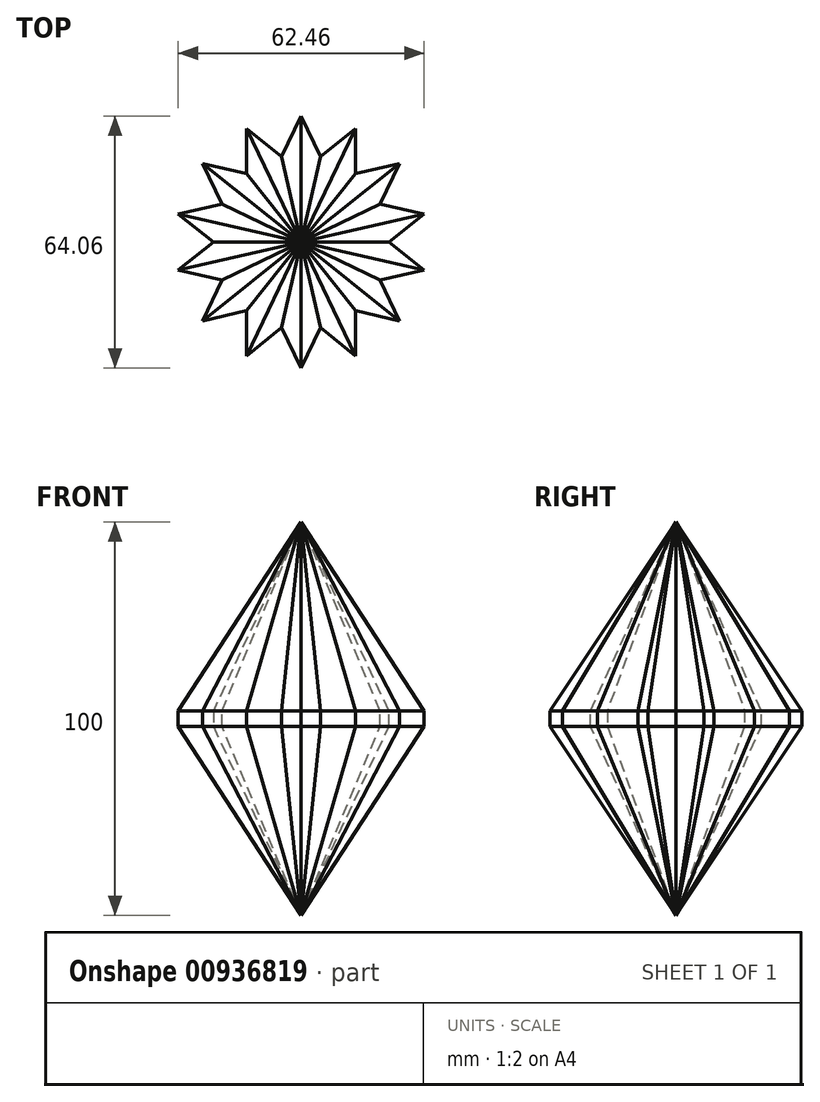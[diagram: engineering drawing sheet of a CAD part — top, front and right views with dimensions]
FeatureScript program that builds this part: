
annotation { "Feature Type Name" : "Feature", "Feature Type Description" : "" }
export const myFeature = defineFeature(function(context is Context, id is Id, definition is map)
    precondition{}
    {
        {
            var Q0;
            Q0=qCreatedBy(makeId("Top.planeOp"),FACE);
            var sketch = newSketch(context, id + "F0", { "sketchPlane" : qUnion([Q0])});
            skCircle(sketch, "E0.cCircle", {"center": v(0, 0) * mm, "radius": 32.03 * mm, "construction": true});
            skLineSegment(sketch, "E0.0", {"start": v(-34.66, -7.91) * mm, "end": v(-27.8, 22.17) * mm, "construction": true});
            skLineSegment(sketch, "E0.1", {"start": v(-27.8, 22.17) * mm, "end": v(0, 35.55) * mm, "construction": true});
            skLineSegment(sketch, "E0.2", {"start": v(0, 35.55) * mm, "end": v(27.8, 22.17) * mm, "construction": true});
            skLineSegment(sketch, "E0.3", {"start": v(27.8, 22.17) * mm, "end": v(34.66, -7.91) * mm, "construction": true});
            skLineSegment(sketch, "E0.4", {"start": v(34.66, -7.91) * mm, "end": v(15.42, -32.03) * mm, "construction": true});
            skLineSegment(sketch, "E0.5", {"start": v(15.42, -32.03) * mm, "end": v(-15.42, -32.03) * mm, "construction": true});
            skLineSegment(sketch, "E0.6", {"start": v(-15.42, -32.03) * mm, "end": v(-34.66, -7.91) * mm, "construction": true});
            skPoint(sketch, "E0.0.midPoint", {"position": v(-31.23, 7.13) * mm});
            skCircle(sketch, "E1.cCircle", {"center": v(0, 0) * mm, "radius": 16 * mm, "construction": true});
            skLineSegment(sketch, "E1.0", {"start": v(-17.32, -3.95) * mm, "end": v(-13.9, 11.08) * mm});
            skLineSegment(sketch, "E1.1", {"start": v(-13.9, 11.08) * mm, "end": v(0, 17.77) * mm, "construction": true});
            skLineSegment(sketch, "E1.2", {"start": v(0, 17.77) * mm, "end": v(13.9, 11.08) * mm});
            skLineSegment(sketch, "E1.3", {"start": v(13.9, 11.08) * mm, "end": v(17.32, -3.95) * mm});
            skLineSegment(sketch, "E1.4", {"start": v(17.32, -3.95) * mm, "end": v(7.7, -16) * mm});
            skLineSegment(sketch, "E1.5", {"start": v(7.7, -16) * mm, "end": v(-7.7, -16) * mm});
            skLineSegment(sketch, "E1.6", {"start": v(-7.7, -16) * mm, "end": v(-17.32, -3.95) * mm});
            skPoint(sketch, "E1.0.midPoint", {"position": v(-15.6, 3.56) * mm});
            skLineSegment(sketch, "E2", {"start": v(0, 17.77) * mm, "end": v(13.9, 28.86) * mm});
            skLineSegment(sketch, "E3", {"start": v(13.9, 28.86) * mm, "end": v(13.9, 11.08) * mm});
            skLineSegment(sketch, "E4", {"start": v(13.9, 11.08) * mm, "end": v(31.23, 7.13) * mm});
            skLineSegment(sketch, "E5", {"start": v(31.23, 7.13) * mm, "end": v(17.32, -3.95) * mm});
            skLineSegment(sketch, "E6", {"start": v(0, 17.77) * mm, "end": v(-13.9, 28.86) * mm});
            skLineSegment(sketch, "E7", {"start": v(-13.9, 28.86) * mm, "end": v(-13.9, 11.08) * mm});
            skLineSegment(sketch, "E8", {"start": v(-13.9, 11.08) * mm, "end": v(-31.23, 7.13) * mm});
            skLineSegment(sketch, "E9", {"start": v(-31.23, 7.13) * mm, "end": v(-17.32, -3.95) * mm});
            skLineSegment(sketch, "E10", {"start": v(-17.32, -3.95) * mm, "end": v(-25.04, -19.97) * mm});
            skLineSegment(sketch, "E11", {"start": v(-25.04, -19.97) * mm, "end": v(-7.7, -16) * mm});
            skLineSegment(sketch, "E12", {"start": v(-7.7, -16) * mm, "end": v(0, -32.03) * mm});
            skLineSegment(sketch, "E13", {"start": v(0, -32.03) * mm, "end": v(7.7, -16) * mm});
            skLineSegment(sketch, "E14", {"start": v(7.7, -16) * mm, "end": v(25.04, -19.97) * mm});
            skLineSegment(sketch, "E15", {"start": v(25.04, -19.97) * mm, "end": v(17.32, -3.95) * mm});
            skSolve(sketch);
        }
        {
            var Q0;
            Q0=qCreatedBy(makeId("Top.planeOp"),FACE);
            cPlane(context, id + "F1", {"entities" : qUnion([Q0]), "cplaneType" : CPlaneType.OFFSET, "offset" : 50 * mm, "width" : 150 * mm, "height" : 150 * mm});
        }
        {
            var Q0;
            Q0=makeQuery(id+"F0.imprint","IMPRINT",FACE,{"disambiguationData":[TD([[makeQuery(id+"F0.imprint","IMPRINT",EDGE,{"derivedFrom":sQuery(id+"F0.wireOp",EDGE,"E1.0")}),-1.0]])]});
            var Q1;
            Q1=makeQuery(id+"F0.imprint","IMPRINT",FACE,{"disambiguationData":[TD([[makeQuery(id+"F0.imprint","IMPRINT",EDGE,{"derivedFrom":sQuery(id+"F0.wireOp",EDGE,"E1.4")}),1.0]])]});
            var Q2;
            Q2=makeQuery(id+"F0.imprint","IMPRINT",FACE,{"disambiguationData":[TD([[makeQuery(id+"F0.imprint","IMPRINT",EDGE,{"derivedFrom":sQuery(id+"F0.wireOp",EDGE,"E1.3")}),1.0]])]});
            var Q3;
            Q3=makeQuery(id+"F0.imprint","IMPRINT",FACE,{"disambiguationData":[TD([[makeQuery(id+"F0.imprint","IMPRINT",EDGE,{"derivedFrom":sQuery(id+"F0.wireOp",EDGE,"E1.5")}),1.0]])]});
            var Q4;
            Q4=makeQuery(id+"F0.imprint","IMPRINT",FACE,{"disambiguationData":[TD([[makeQuery(id+"F0.imprint","IMPRINT",EDGE,{"derivedFrom":sQuery(id+"F0.wireOp",EDGE,"E1.6")}),1.0]])]});
            var Q5;
            Q5=makeQuery(id+"F0.imprint","IMPRINT",FACE,{"disambiguationData":[TD([[makeQuery(id+"F0.imprint","IMPRINT",EDGE,{"derivedFrom":sQuery(id+"F0.wireOp",EDGE,"E1.0")}),1.0]])]});
            var Q6;
            Q6=makeQuery(id+"F0.imprint","IMPRINT",FACE,{"disambiguationData":[TD([[makeQuery(id+"F0.imprint","IMPRINT",EDGE,{"derivedFrom":sQuery(id+"F0.wireOp",EDGE,"E1.2")}),1.0]])]});
            extrude(context, id + "F2", {"entities" : qUnion([Q0, Q1, Q2, Q3, Q4, Q5, Q6]), "depth" : 2 * mm, "offsetDistance" : 25 * mm});
        }
        {
            var Q0;
            Q0=qCreatedBy(id+"F1.planeOp",FACE);
            var sketch = newSketch(context, id + "F3", { "sketchPlane" : qUnion([Q0])});
            skCircle(sketch, "E16", {"center": v(0, 0) * mm, "radius": 2.5 * mm});
            skSolve(sketch);
        }
        {
            var Q1;
            Q1=sQuery(id+"F3.wireOp",VERTEX,"E16.center");
            var Q2;
            Q2=makeQuery(id+"F2.opExtrude","CAP_FACE",FACE,{"disambiguationData":[OSD([sQuery(id+"F0.wireOp",EDGE,"E2"),sQuery(id+"F0.wireOp",EDGE,"E3"),sQuery(id+"F0.wireOp",EDGE,"E4"),sQuery(id+"F0.wireOp",EDGE,"E5"),sQuery(id+"F0.wireOp",EDGE,"E6"),sQuery(id+"F0.wireOp",EDGE,"E7"),sQuery(id+"F0.wireOp",EDGE,"E8"),sQuery(id+"F0.wireOp",EDGE,"E9"),sQuery(id+"F0.wireOp",EDGE,"E10"),sQuery(id+"F0.wireOp",EDGE,"E11"),sQuery(id+"F0.wireOp",EDGE,"E12"),sQuery(id+"F0.wireOp",EDGE,"E13"),sQuery(id+"F0.wireOp",EDGE,"E14"),sQuery(id+"F0.wireOp",EDGE,"E15")])],"isStart":false});
            loft(context, id + "F4", {"operationType" : NewBodyOperationType.ADD, "sheetProfilesArray" : [{ "sheetProfileEntities" : qUnion([Q1]) }, { "sheetProfileEntities" : qUnion([Q2]) }]});
        }
        {
            var Q0;
            Q0=makeQuery(id+"F2.opExtrude","SWEPT_BODY",BODY,{"disambiguationData":[OSD([sQuery(id+"F0.wireOp",EDGE,"E2"),sQuery(id+"F0.wireOp",EDGE,"E3"),sQuery(id+"F0.wireOp",EDGE,"E4"),sQuery(id+"F0.wireOp",EDGE,"E5"),sQuery(id+"F0.wireOp",EDGE,"E6"),sQuery(id+"F0.wireOp",EDGE,"E7"),sQuery(id+"F0.wireOp",EDGE,"E8"),sQuery(id+"F0.wireOp",EDGE,"E9"),sQuery(id+"F0.wireOp",EDGE,"E10"),sQuery(id+"F0.wireOp",EDGE,"E11"),sQuery(id+"F0.wireOp",EDGE,"E12"),sQuery(id+"F0.wireOp",EDGE,"E13"),sQuery(id+"F0.wireOp",EDGE,"E14"),sQuery(id+"F0.wireOp",EDGE,"E15")])]});
            var Q1;
            Q1=makeQuery(id+"F2.opExtrude","CAP_FACE",FACE,{"disambiguationData":[OSD([sQuery(id+"F0.wireOp",EDGE,"E2"),sQuery(id+"F0.wireOp",EDGE,"E3"),sQuery(id+"F0.wireOp",EDGE,"E4"),sQuery(id+"F0.wireOp",EDGE,"E5"),sQuery(id+"F0.wireOp",EDGE,"E6"),sQuery(id+"F0.wireOp",EDGE,"E7"),sQuery(id+"F0.wireOp",EDGE,"E8"),sQuery(id+"F0.wireOp",EDGE,"E9"),sQuery(id+"F0.wireOp",EDGE,"E10"),sQuery(id+"F0.wireOp",EDGE,"E11"),sQuery(id+"F0.wireOp",EDGE,"E12"),sQuery(id+"F0.wireOp",EDGE,"E13"),sQuery(id+"F0.wireOp",EDGE,"E14"),sQuery(id+"F0.wireOp",EDGE,"E15")])],"isStart":true});
            mirror(context, id + "F5", {"operationType" : NewBodyOperationType.ADD, "entities" : qUnion([Q0]), "mirrorPlane" : qUnion([Q1])});
        }
        {
            var Q0;
            Q0=makeQuery(id+"F2.opExtrude","SWEPT_BODY",BODY,{"disambiguationData":[OSD([sQuery(id+"F0.wireOp",EDGE,"E2"),sQuery(id+"F0.wireOp",EDGE,"E3"),sQuery(id+"F0.wireOp",EDGE,"E4"),sQuery(id+"F0.wireOp",EDGE,"E5"),sQuery(id+"F0.wireOp",EDGE,"E6"),sQuery(id+"F0.wireOp",EDGE,"E7"),sQuery(id+"F0.wireOp",EDGE,"E8"),sQuery(id+"F0.wireOp",EDGE,"E9"),sQuery(id+"F0.wireOp",EDGE,"E10"),sQuery(id+"F0.wireOp",EDGE,"E11"),sQuery(id+"F0.wireOp",EDGE,"E12"),sQuery(id+"F0.wireOp",EDGE,"E13"),sQuery(id+"F0.wireOp",EDGE,"E14"),sQuery(id+"F0.wireOp",EDGE,"E15")])]});
            var Q1;
            Q1=qCreatedBy(makeId("Front.planeOp"),FACE);
            mirror(context, id + "F6", {"operationType" : NewBodyOperationType.ADD, "entities" : qUnion([Q0]), "mirrorPlane" : qUnion([Q1])});
        }
    });
